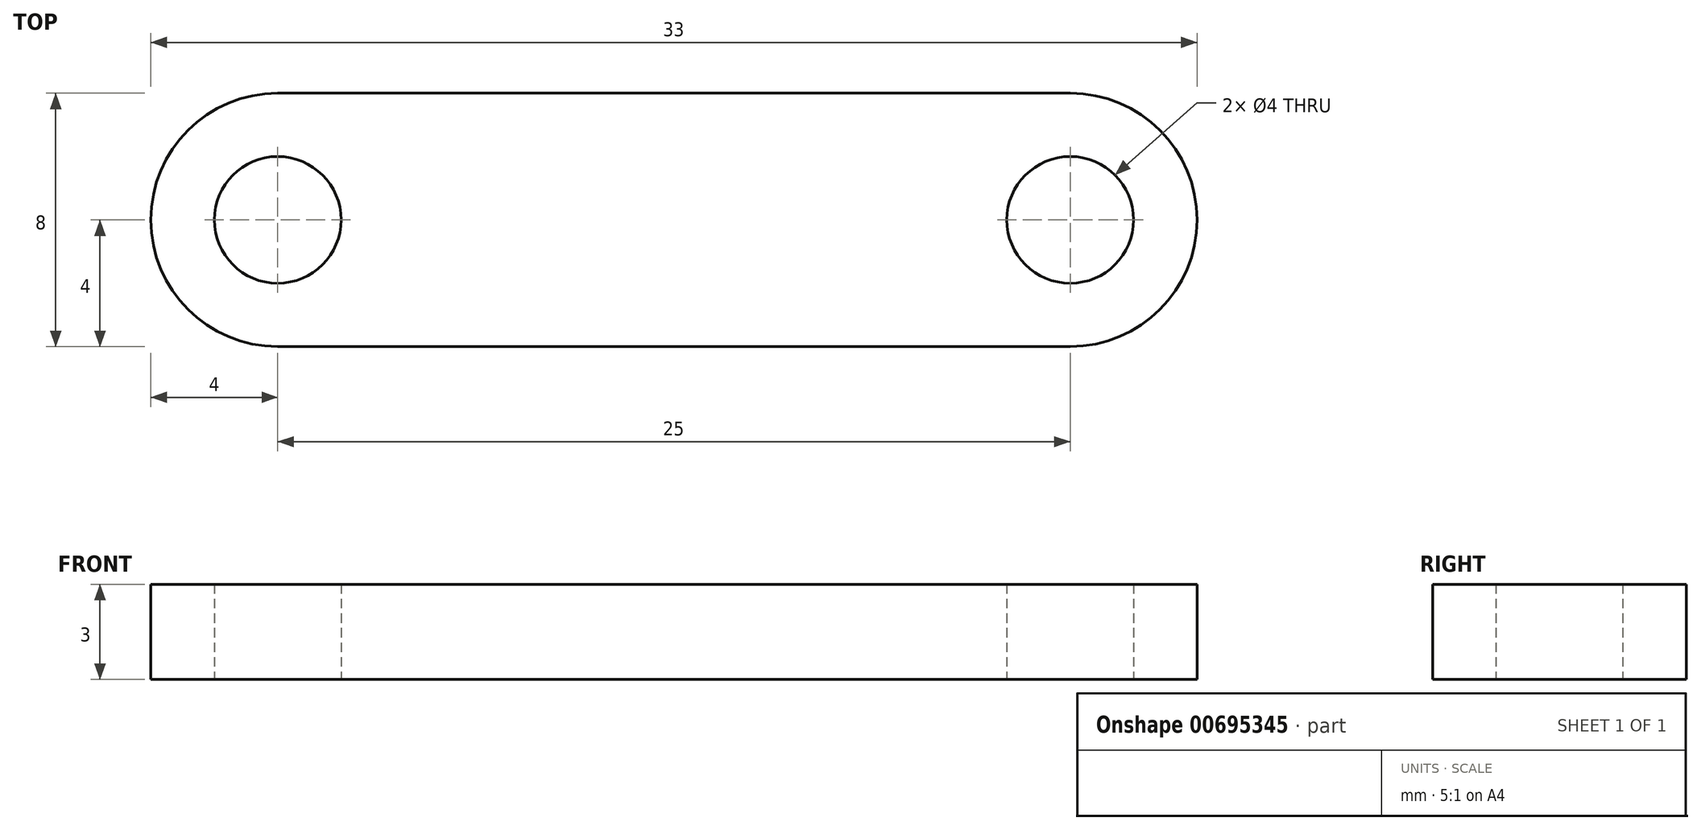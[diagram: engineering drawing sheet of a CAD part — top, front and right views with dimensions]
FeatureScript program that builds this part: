
annotation { "Feature Type Name" : "Feature", "Feature Type Description" : "" }
export const myFeature = defineFeature(function(context is Context, id is Id, definition is map)
    precondition{}
    {
        {
            var Q0;
            Q0=qCreatedBy(makeId("Top.planeOp"),FACE);
            var sketch = newSketch(context, id + "F0", { "sketchPlane" : qUnion([Q0])});
            skLineSegment(sketch, "E0.bottom", {"start": v(12.5, -4) * mm, "end": v(-12.5, -4) * mm});
            skLineSegment(sketch, "E0.top", {"start": v(12.5, 4) * mm, "end": v(-12.5, 4) * mm});
            skLineSegment(sketch, "E0.left", {"start": v(12.5, -4) * mm, "end": v(12.5, 4) * mm});
            skLineSegment(sketch, "E0.right", {"start": v(-12.5, -4) * mm, "end": v(-12.5, 4) * mm});
            skPoint(sketch, "E0.middle", {"position": v(0, 0) * mm});
            skCircle(sketch, "E1", {"center": v(-12.5, 0) * mm, "radius": 4 * mm});
            skCircle(sketch, "E2", {"center": v(12.5, 0) * mm, "radius": 4 * mm});
            skCircle(sketch, "E3", {"center": v(12.5, 0) * mm, "radius": 2 * mm});
            skCircle(sketch, "E4", {"center": v(-12.5, 0) * mm, "radius": 2 * mm});
            skSolve(sketch);
        }
        {
            var Q0;
            Q0 = qSketchRegion(id + "F0", true);
            extrude(context, id + "F1", {"entities" : qUnion([Q0]), "depth" : 3 * mm, "offsetDistance" : 25 * mm});
        }
    });
